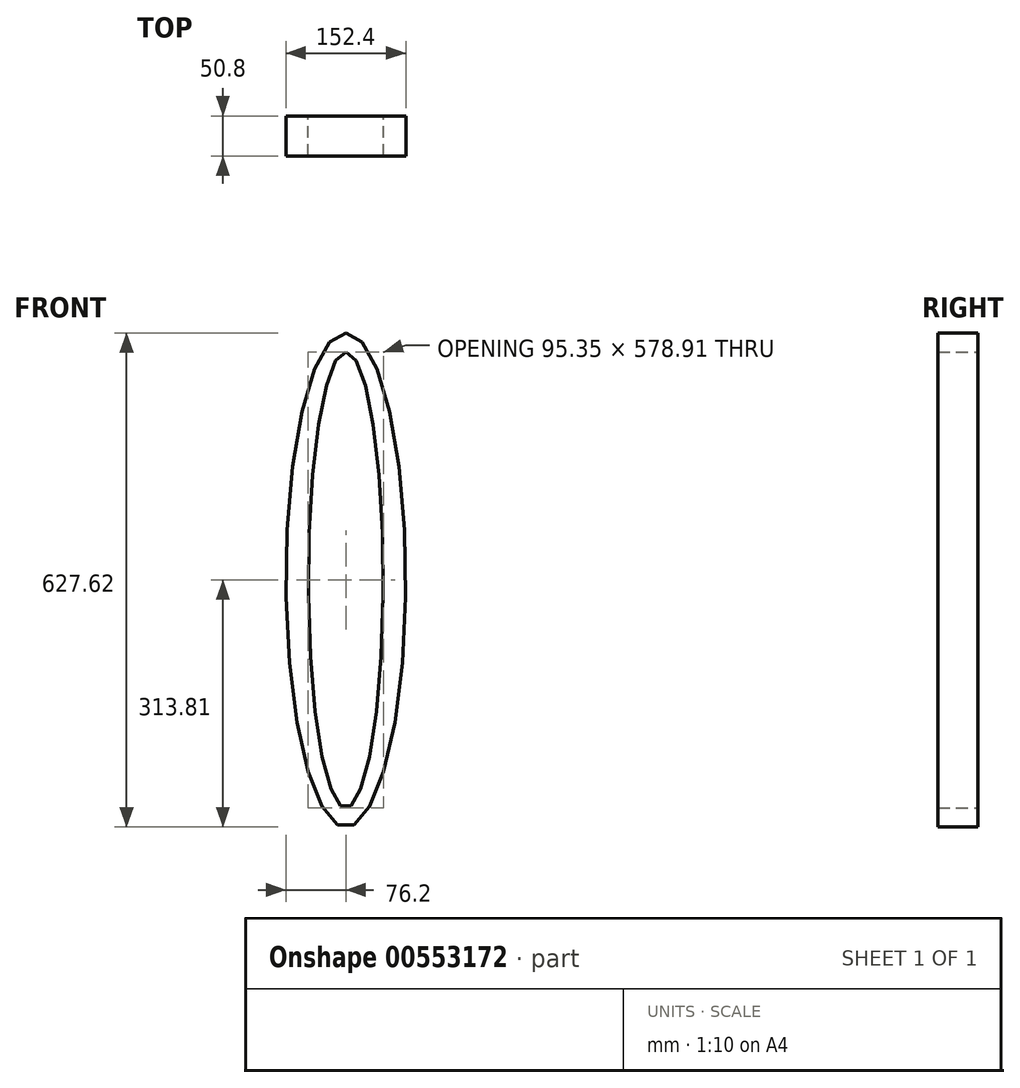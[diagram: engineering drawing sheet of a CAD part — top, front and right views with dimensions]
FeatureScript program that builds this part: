
annotation { "Feature Type Name" : "Feature", "Feature Type Description" : "" }
export const myFeature = defineFeature(function(context is Context, id is Id, definition is map)
    precondition{}
    {
        {
            var Q0;
            Q0=qCreatedBy(makeId("Front.planeOp"),FACE);
            var sketch = newSketch(context, id + "F0", { "sketchPlane" : qUnion([Q0])});
            skEllipse(sketch, "E0", {"center": v(0, 0) * mm, "majorRadius": 313.8 * mm, "minorRadius": 76.2 * mm, "majorAxis": v(0, 1)});
            skEllipse(sketch, "E1", {"center": v(0, 0) * mm, "majorRadius": 289.46 * mm, "minorRadius": 47.68 * mm, "majorAxis": v(0, 1)});
            skSolve(sketch);
        }
        {
            var Q0;
            Q0=makeQuery(id+"F0.imprint","IMPRINT",FACE,{"disambiguationData":[TD([[makeQuery(id+"F0.imprint","IMPRINT",EDGE,{"derivedFrom":sQuery(id+"F0.wireOp",EDGE,"E0")}),1.0]])]});
            extrude(context, id + "F1", {"entities" : qUnion([Q0]), "depth" : 50.8 * mm, "offsetDistance" : 25.4 * mm});
        }
    });
